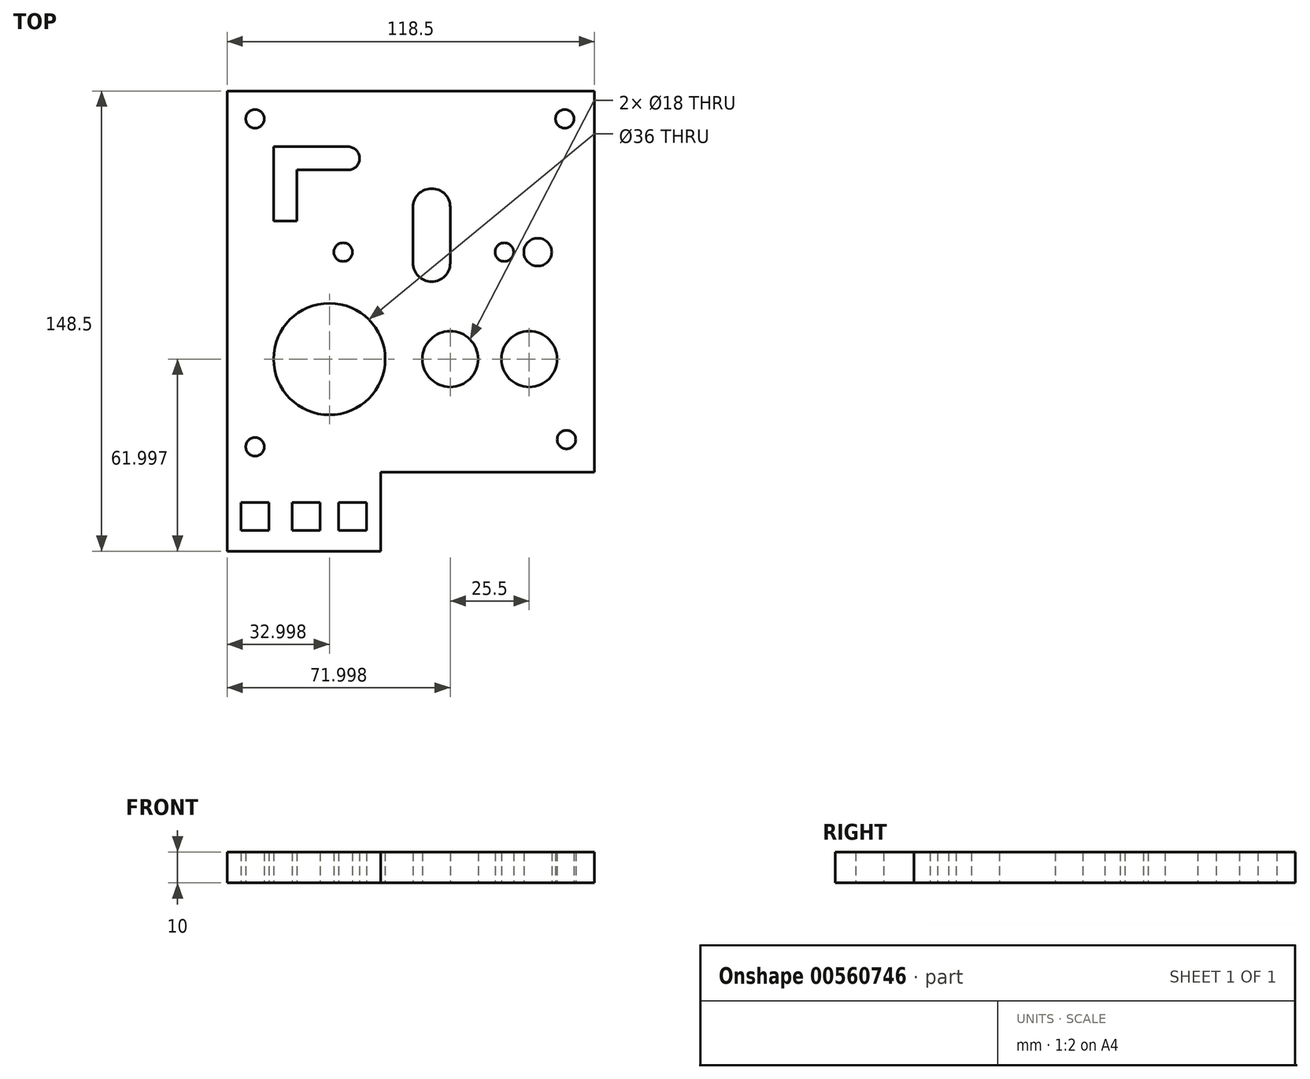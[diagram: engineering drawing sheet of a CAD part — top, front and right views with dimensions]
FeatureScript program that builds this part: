
annotation { "Feature Type Name" : "Feature", "Feature Type Description" : "" }
export const myFeature = defineFeature(function(context is Context, id is Id, definition is map)
    precondition{}
    {
        {
            var Q0;
            Q0=qCreatedBy(makeId("Top.planeOp"),FACE);
            var sketch = newSketch(context, id + "F0", { "sketchPlane" : qUnion([Q0])});
            skLineSegment(sketch, "E0", {"start": v(-69.22, 69.5) * mm, "end": v(49.28, 69.5) * mm});
            skLineSegment(sketch, "E1", {"start": v(49.28, 69.5) * mm, "end": v(49.28, -53.5) * mm});
            skLineSegment(sketch, "E2", {"start": v(49.28, -53.5) * mm, "end": v(-19.72, -53.5) * mm});
            skLineSegment(sketch, "E3", {"start": v(-19.72, -53.5) * mm, "end": v(-19.72, -79) * mm});
            skLineSegment(sketch, "E4", {"start": v(-19.72, -79) * mm, "end": v(-69.22, -79) * mm});
            skLineSegment(sketch, "E5", {"start": v(-69.22, -79) * mm, "end": v(-69.22, 69.5) * mm});
            skCircle(sketch, "E6", {"center": v(39.73, 60.5) * mm, "radius": 3 * mm});
            skCircle(sketch, "E7", {"center": v(-60.22, 60.5) * mm, "radius": 3 * mm});
            skCircle(sketch, "E8", {"center": v(40.28, -42.96) * mm, "radius": 3 * mm});
            skCircle(sketch, "E9", {"center": v(-60.22, -45.3) * mm, "radius": 3 * mm});
            skLineSegment(sketch, "E10", {"start": v(-54.22, 51.5) * mm, "end": v(-30.22, 51.5) * mm});
            skLineSegment(sketch, "E11", {"start": v(-54.22, 51.5) * mm, "end": v(-54.22, 27.5) * mm});
            skLineSegment(sketch, "E12", {"start": v(-54.22, 27.5) * mm, "end": v(-46.72, 27.5) * mm});
            skLineSegment(sketch, "E13", {"start": v(-46.72, 27.5) * mm, "end": v(-46.72, 44) * mm});
            skLineSegment(sketch, "E14", {"start": v(-46.72, 44) * mm, "end": v(-30.22, 44) * mm});
            skArc(sketch, "E15", {"start": v(-30.22, 44) * mm, "mid": v(-26.47, 47.76) * mm, "end": v(-30.22, 51.5) * mm});
            skLineSegment(sketch, "E16.bottom", {"start": v(-64.72, -63.3) * mm, "end": v(-55.72, -63.3) * mm});
            skLineSegment(sketch, "E16.top", {"start": v(-64.72, -72.3) * mm, "end": v(-55.72, -72.3) * mm});
            skLineSegment(sketch, "E16.left", {"start": v(-64.72, -63.3) * mm, "end": v(-64.72, -72.3) * mm});
            skLineSegment(sketch, "E16.right", {"start": v(-55.72, -63.3) * mm, "end": v(-55.72, -72.3) * mm});
            skLineSegment(sketch, "E17.bottom", {"start": v(-48.22, -63.3) * mm, "end": v(-39.22, -63.3) * mm});
            skLineSegment(sketch, "E17.top", {"start": v(-48.22, -72.3) * mm, "end": v(-39.22, -72.3) * mm});
            skLineSegment(sketch, "E17.left", {"start": v(-48.22, -63.3) * mm, "end": v(-48.22, -72.3) * mm});
            skLineSegment(sketch, "E17.right", {"start": v(-39.22, -63.3) * mm, "end": v(-39.22, -72.3) * mm});
            skLineSegment(sketch, "E18.bottom", {"start": v(-33.22, -63.3) * mm, "end": v(-24.22, -63.3) * mm});
            skLineSegment(sketch, "E18.top", {"start": v(-33.22, -72.3) * mm, "end": v(-24.22, -72.3) * mm});
            skLineSegment(sketch, "E18.left", {"start": v(-33.22, -63.3) * mm, "end": v(-33.22, -72.3) * mm});
            skLineSegment(sketch, "E18.right", {"start": v(-24.22, -63.3) * mm, "end": v(-24.22, -72.3) * mm});
            skLineSegment(sketch, "E19", {"start": v(-9.22, 32) * mm, "end": v(-9.22, 14) * mm});
            skLineSegment(sketch, "E20", {"start": v(2.78, 32) * mm, "end": v(2.78, 14) * mm});
            skArc(sketch, "E21", {"start": v(2.78, 32) * mm, "mid": v(-3.22, 38) * mm, "end": v(-9.22, 32) * mm});
            skArc(sketch, "E22", {"start": v(-9.22, 14) * mm, "mid": v(-3.22, 8) * mm, "end": v(2.78, 14) * mm});
            skLineSegment(sketch, "E23", {"start": v(40.28, -66.66) * mm, "end": v(28.28, -66.66) * mm});
            skCircle(sketch, "E24", {"center": v(28.28, -17) * mm, "radius": 9 * mm});
            skCircle(sketch, "E25", {"center": v(2.78, -17) * mm, "radius": 9 * mm});
            skCircle(sketch, "E26", {"center": v(-36.22, -17) * mm, "radius": 18 * mm});
            skLineSegment(sketch, "E27", {"start": v(61.22, 69.5) * mm, "end": v(61.22, 17.5) * mm});
            skLineSegment(sketch, "E28", {"start": v(39.73, 78.65) * mm, "end": v(20.23, 78.65) * mm});
            skCircle(sketch, "E29", {"center": v(20.23, 17.5) * mm, "radius": 3 * mm});
            skCircle(sketch, "E30", {"center": v(31.01, 17.5) * mm, "radius": 4.5 * mm});
            skCircle(sketch, "E31", {"center": v(-31.78, 17.5) * mm, "radius": 3 * mm});
            skSolve(sketch);
        }
        {
            var Q0;
            Q0=makeQuery(id+"F0.imprint","IMPRINT",FACE,{"disambiguationData":[TD([[makeQuery(id+"F0.imprint","IMPRINT",EDGE,{"derivedFrom":sQuery(id+"F0.wireOp",EDGE,"E0")}),-1.0]])]});
            extrude(context, id + "F1", {"entities" : qUnion([Q0]), "depth" : 10 * mm, "offsetDistance" : 25 * mm});
        }
    });
